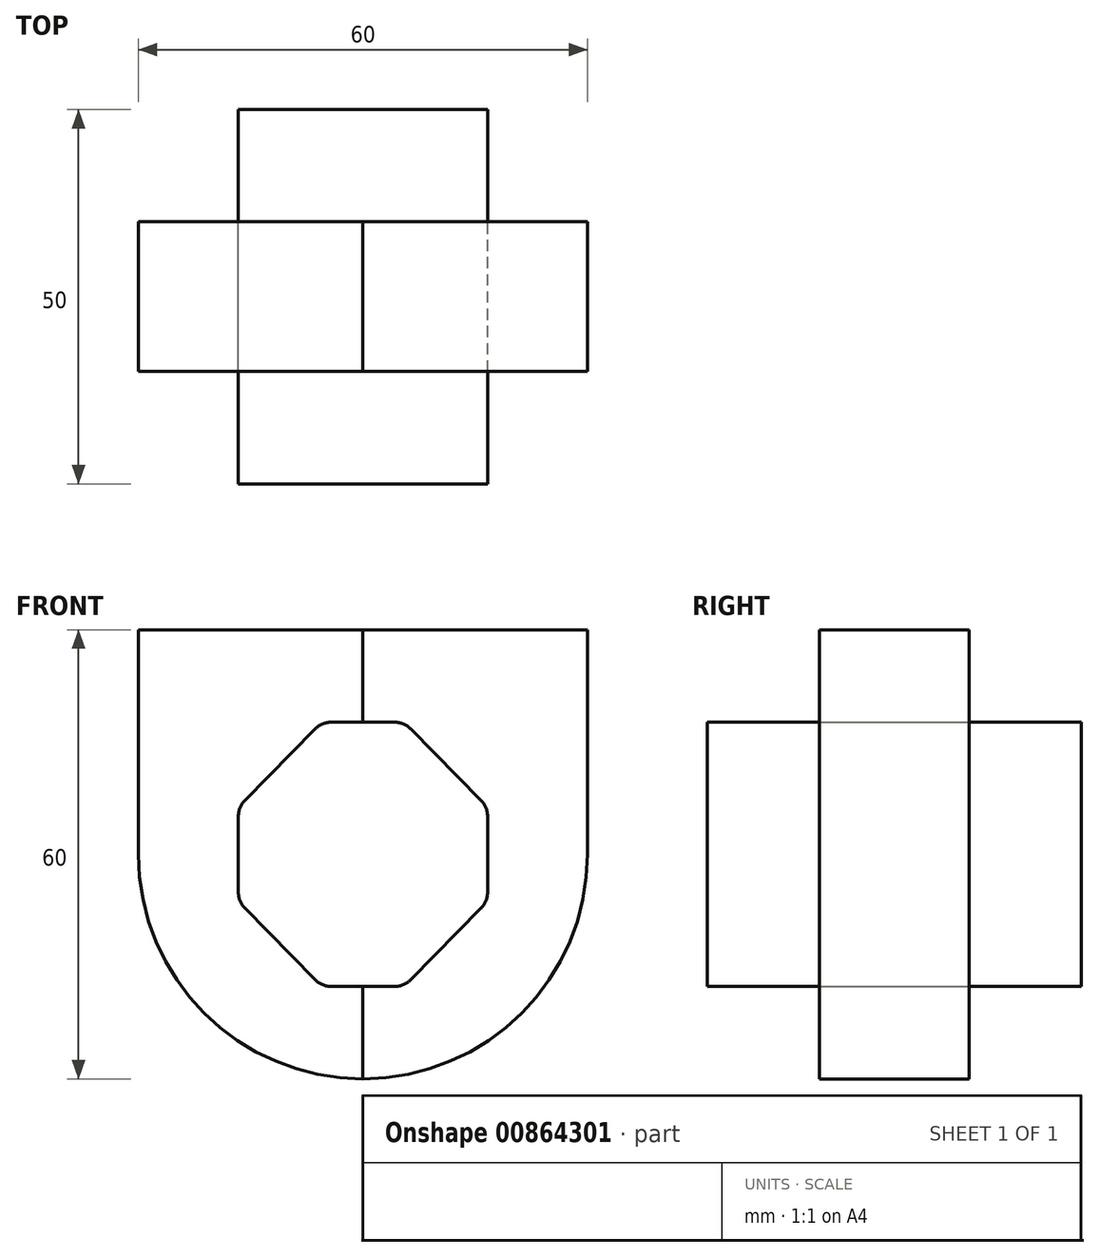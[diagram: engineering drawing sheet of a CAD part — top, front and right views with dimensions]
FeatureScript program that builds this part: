
annotation { "Feature Type Name" : "Feature", "Feature Type Description" : "" }
export const myFeature = defineFeature(function(context is Context, id is Id, definition is map)
    precondition{}
    {
        {
            var Q0;
            Q0=qCreatedBy(makeId("Front.planeOp"),FACE);
            var sketch = newSketch(context, id + "F0", { "sketchPlane" : qUnion([Q0])});
            skLineSegment(sketch, "E0", {"start": v(-16.65, 5.1) * mm, "end": v(-16.65, -5.1) * mm});
            skLineSegment(sketch, "E1", {"start": v(16.65, 5.1) * mm, "end": v(16.65, -5.1) * mm});
            skLineSegment(sketch, "E2", {"start": v(-4.24, 17.65) * mm, "end": v(4.24, 17.65) * mm});
            skLineSegment(sketch, "E3", {"start": v(-4.24, -17.65) * mm, "end": v(4.24, -17.65) * mm});
            skLineSegment(sketch, "E4", {"start": v(-15.79, 7.2) * mm, "end": v(-6.38, 16.75) * mm});
            skLineSegment(sketch, "E5", {"start": v(6.38, -16.75) * mm, "end": v(15.79, -7.2) * mm});
            skLineSegment(sketch, "E6", {"start": v(-15.79, -7.2) * mm, "end": v(-6.38, -16.75) * mm});
            skLineSegment(sketch, "E7", {"start": v(6.38, 16.75) * mm, "end": v(15.79, 7.2) * mm});
            skPoint(sketch, "E8.visualSharp", {"position": v(-5.5, 17.65) * mm});
            skArc(sketch, "E8.filletArc", {"start": v(-4.24, 17.65) * mm, "mid": v(-5.4, 17.42) * mm, "end": v(-6.38, 16.75) * mm});
            skPoint(sketch, "E9.visualSharp", {"position": v(5.5, 17.65) * mm});
            skArc(sketch, "E9.filletArc", {"start": v(6.38, 16.75) * mm, "mid": v(5.4, 17.42) * mm, "end": v(4.24, 17.65) * mm});
            skPoint(sketch, "E10.visualSharp", {"position": v(16.65, 6.32) * mm});
            skArc(sketch, "E10.filletArc", {"start": v(16.65, 5.1) * mm, "mid": v(16.43, 6.23) * mm, "end": v(15.79, 7.2) * mm});
            skPoint(sketch, "E11.visualSharp", {"position": v(16.65, -6.32) * mm});
            skArc(sketch, "E11.filletArc", {"start": v(15.79, -7.2) * mm, "mid": v(16.43, -6.23) * mm, "end": v(16.65, -5.1) * mm});
            skPoint(sketch, "E12.visualSharp", {"position": v(5.5, -17.65) * mm});
            skArc(sketch, "E12.filletArc", {"start": v(4.24, -17.65) * mm, "mid": v(5.4, -17.42) * mm, "end": v(6.38, -16.75) * mm});
            skPoint(sketch, "E13.visualSharp", {"position": v(-5.5, -17.65) * mm});
            skArc(sketch, "E13.filletArc", {"start": v(-6.38, -16.75) * mm, "mid": v(-5.4, -17.42) * mm, "end": v(-4.24, -17.65) * mm});
            skPoint(sketch, "E14.visualSharp", {"position": v(-16.65, -6.32) * mm});
            skArc(sketch, "E14.filletArc", {"start": v(-16.65, -5.1) * mm, "mid": v(-16.43, -6.23) * mm, "end": v(-15.79, -7.2) * mm});
            skPoint(sketch, "E15.visualSharp", {"position": v(-16.65, 6.32) * mm});
            skArc(sketch, "E15.filletArc", {"start": v(-15.79, 7.2) * mm, "mid": v(-16.43, 6.23) * mm, "end": v(-16.65, 5.1) * mm});
            skLineSegment(sketch, "E16", {"start": v(0, 17.65) * mm, "end": v(0, -17.65) * mm, "construction": true});
            skLineSegment(sketch, "E17", {"start": v(-16.65, 0) * mm, "end": v(16.65, 0) * mm, "construction": true});
            skCircle(sketch, "E18", {"center": v(0, 0) * mm, "radius": 30 * mm});
            skLineSegment(sketch, "E19", {"start": v(-30, 0) * mm, "end": v(-30, 30) * mm});
            skLineSegment(sketch, "E20", {"start": v(-30, 30) * mm, "end": v(30, 30) * mm});
            skLineSegment(sketch, "E21", {"start": v(30, 30) * mm, "end": v(30, 0) * mm});
            skLineSegment(sketch, "E22", {"start": v(0, 30) * mm, "end": v(0, 17.65) * mm});
            skLineSegment(sketch, "E23", {"start": v(0, -17.65) * mm, "end": v(0, -30) * mm});
            skSolve(sketch);
        }
        {
            var Q0;
            Q0=makeQuery(id+"F0.imprint","IMPRINT",FACE,{"disambiguationData":[TD([[makeQuery(id+"F0.imprint","IMPRINT",EDGE,{"derivedFrom":sQuery(id+"F0.wireOp",EDGE,"E0")}),1.0]])]});
            extrude(context, id + "F1", {"entities" : qUnion([Q0]), "depth" : 25 * mm, "offsetDistance" : 25 * mm, "hasSecondDirection" : true, "secondDirectionOppositeDirection" : true, "secondDirectionDepth" : 25 * mm});
        }
        {
            var Q0;
            {var subQ0=sQuery(id+"F0.wireOp",EDGE,"E19");Q0=makeQuery(id+"F0.imprint","IMPRINT",FACE,{"disambiguationData":[TD([[makeQuery(id+"F0.imprint","IMPRINT",EDGE,{"derivedFrom":subQ0}),-1.0]])]});}
            var Q1;
            Q1=makeQuery(id+"F0.imprint","IMPRINT",FACE,{"disambiguationData":[TD([[makeQuery(id+"F0.imprint","IMPRINT",EDGE,{"derivedFrom":sQuery(id+"F0.wireOp",EDGE,"E0")}),-1.0]])]});
            extrude(context, id + "F2", {"entities" : qUnion([Q0, Q1]), "depth" : 10 * mm, "offsetDistance" : 25 * mm, "hasSecondDirection" : true, "secondDirectionOppositeDirection" : true, "secondDirectionDepth" : 10 * mm});
        }
        {
            var Q0;
            {var subQ0=sQuery(id+"F0.wireOp",EDGE,"E21");Q0=makeQuery(id+"F0.imprint","IMPRINT",FACE,{"disambiguationData":[TD([[makeQuery(id+"F0.imprint","IMPRINT",EDGE,{"derivedFrom":subQ0}),-1.0]])]});}
            var Q1;
            Q1=makeQuery(id+"F0.imprint","IMPRINT",FACE,{"disambiguationData":[TD([[makeQuery(id+"F0.imprint","IMPRINT",EDGE,{"derivedFrom":sQuery(id+"F0.wireOp",EDGE,"E1")}),1.0]])]});
            extrude(context, id + "F3", {"entities" : qUnion([Q0, Q1]), "depth" : 10 * mm, "offsetDistance" : 25 * mm, "hasSecondDirection" : true, "secondDirectionOppositeDirection" : true, "secondDirectionDepth" : 10 * mm});
        }
    });
